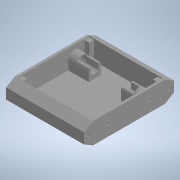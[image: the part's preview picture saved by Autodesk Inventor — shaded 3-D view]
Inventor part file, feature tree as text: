
AUTODESK INVENTOR PART (.ipt)
format: ipt  version: 2020 (Build 240168000, 168)  size: 266,752 bytes
history: native  units: in
note: dims shown in document units (in); Inventor stores cm internally (conversion verified against a paired STEP export)
features: extrude x8, sketch x8, projected_geometry x4, mirror x3
ambient origin geometry x8: Origin, YZ Plane, XZ Plane, XY Plane, X Axis, Y Axis, Z Axis, Center Point
bodies: Solid1 (feature_tree)
feature tree (23):
  extrude  "Extrusion1"  Depth=5.9055in
  extrude  "Extrusion2"  TaperAngle=0.0deg  [1 undecoded]
  extrude  "Extrusion3"  Depth=1.2598in
  extrude  "Extrusion4"  Depth=0.315in
  extrude  "Extrusion5"  TaperAngle=0.0deg  [1 undecoded]
  extrude  "Extrusion6"  Depth=0.689in
  mirror  "Mirror1"
  extrude  "Extrusion7"  Depth=0.0787in
  mirror  "Mirror2"
  extrude  "Extrusion8"  Depth=0.2756in
  mirror  "Mirror3"
  sketch  "Sketch1"  dims[d0=1.378in d1=5.9055in]
  sketch  "Sketch2"  dims[d2=5.1181in d3=0.0in]
  projected_geometry  "Projected Loop1"
  sketch  "Sketch3"  dims[d4=0.1575in d5=1.2598in]
  projected_geometry  "Projected Loop2"
  projected_geometry  "Projected Loop3"
  sketch  "Sketch4"  dims[d6=0.0in d8=0.315in]
  sketch  "Sketch5"  dims[d10=1.1898in d11=0.0in]
  projected_geometry  "Projected Loop4"
  sketch  "Sketch6"  dims[d12=0.6496in d13=0.689in]
  sketch  "Sketch7"  dims[d14=1.5748in d15=0.0787in]
  sketch  "Sketch9"  dims[d16=0.5512in d17=0.0in d18=0.6102in d19=0.4803in d20=0.7874in d21=0.0in d22=0.1654in d23=6.063in d24=0.0in d25=0.5967in d26=0.1575in d27=1.5748in d28=0.0in d29=0.0in d30=0.1575in d31=0.2756in d32=0.0in]
note: 2 required parameter values undecoded (feature->parameter linkage not recoverable at this tier; creation-order binding heuristic only, values carry confidence <= 0.55)
